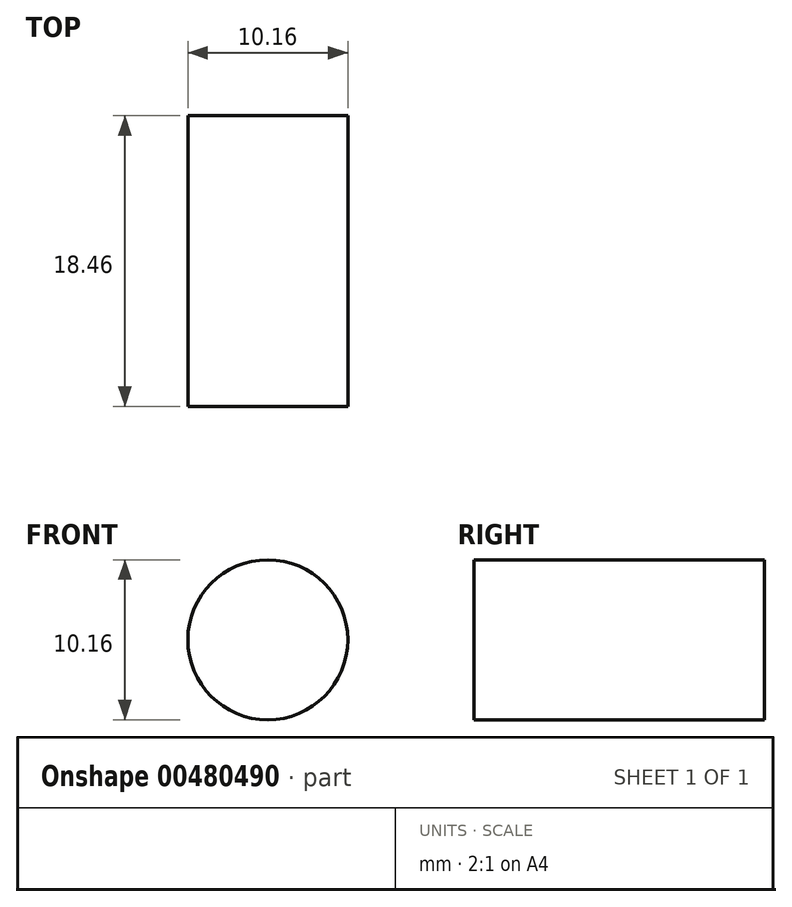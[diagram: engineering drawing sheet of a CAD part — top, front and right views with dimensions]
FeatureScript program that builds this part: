
annotation { "Feature Type Name" : "Feature", "Feature Type Description" : "" }
export const myFeature = defineFeature(function(context is Context, id is Id, definition is map)
    precondition{}
    {
        {
            var Q0;
            Q0=qCreatedBy(makeId("Front.planeOp"),FACE);
            var sketch = newSketch(context, id + "F0", { "sketchPlane" : qUnion([Q0])});
            skCircle(sketch, "E0", {"center": v(0, 0) * mm, "radius": 5.08 * mm});
            skSolve(sketch);
        }
        {
            var Q0;
            Q0 = qSketchRegion(id + "F0", true);
            extrude(context, id + "F1", {"entities" : qUnion([Q0]), "depth" : 18.46 * mm});
        }
    });
